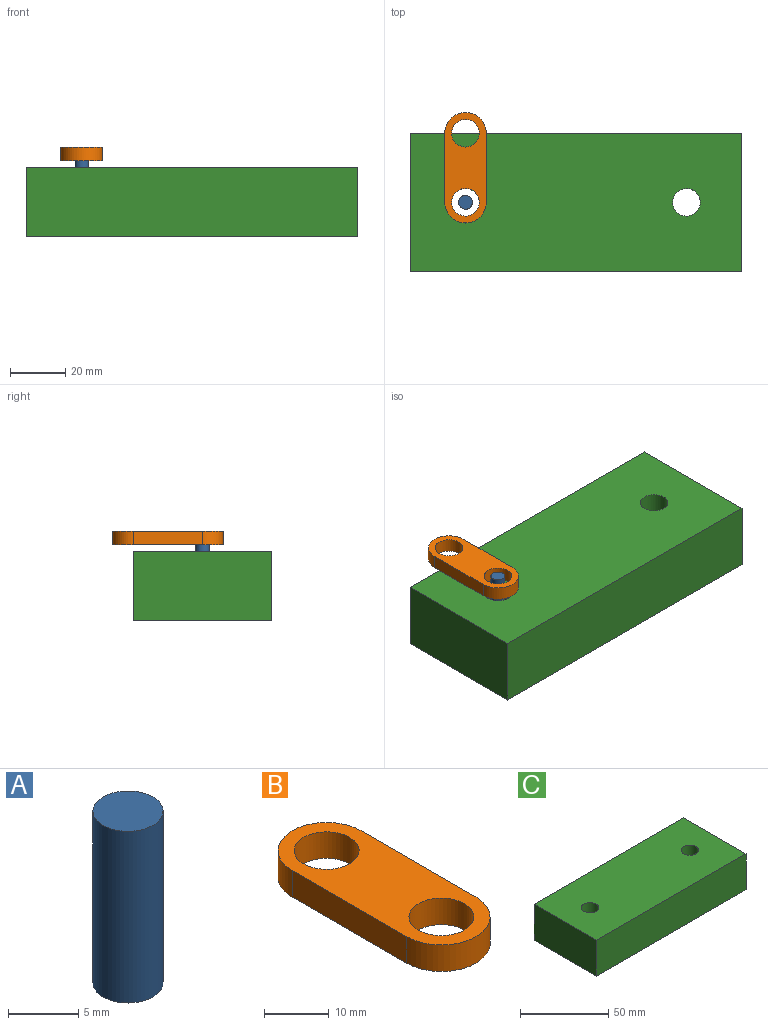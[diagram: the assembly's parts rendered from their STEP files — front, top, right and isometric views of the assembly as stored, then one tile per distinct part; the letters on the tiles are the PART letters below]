
ASSEMBLY  parts=3 mates=2
PART A: 3 faces, bbox 5x5x15 mm
  f0: plane 5x5mm, normal (0,0,-1), area 19.6mm2, adj f1
  f1: cylinder r=2.5mm len=15mm, axis (0,0,1), area 235.6mm2, adj f0,f2
  f2: plane 5x5mm, normal (0,0,1), area 19.6mm2, adj f1
PART B: 8 faces, bbox 15x40x5 mm
  f0: plane 25x5mm, normal (-1,0,0), area 125mm2, adj f1,f5,f6,f7
  f1: cylinder r=7.5mm len=15mm, axis (0,0,-1), area 117.8mm2, adj f0,f2,f6,f7
  f2: plane 25x5mm, normal (1,0,0), area 125mm2, adj f1,f5,f6,f7
  f3: cylinder r=5mm len=10mm, axis (0,0,-1), area 157.1mm2, adj f6,f7
  f4: cylinder r=5mm len=10mm, axis (0,0,-1), area 157.1mm2, adj f6,f7
  f5: cylinder r=7.5mm len=15mm, axis (0,0,-1), area 117.8mm2, adj f0,f2,f6,f7
  f6: plane 40x15mm, normal (0,0,1), area 394.6mm2, adj f0,f1,f2,f3,f4,f5
  f7: plane 40x15mm, normal (0,0,-1), area 394.6mm2, adj f0,f1,f2,f3,f4,f5
PART C: 8 faces, bbox 120x50x25 mm
  f0: plane 50x25mm, normal (1,0,0), area 1250mm2, adj f1,f4,f6,f7
  f1: plane 120x25mm, normal (0,1,0), area 3000mm2, adj f0,f2,f6,f7
  f2: plane 50x25mm, normal (-1,0,0), area 1250mm2, adj f1,f4,f6,f7
  f3: cylinder r=5mm len=25mm, axis (0,0,-1), area 785.4mm2, adj f6,f7
  f4: plane 120x25mm, normal (0,-1,0), area 3000mm2, adj f0,f2,f6,f7
  f5: cylinder r=5mm len=25mm, axis (0,0,-1), area 785.4mm2, adj f6,f7
  f6: plane 120x50mm, normal (0,0,1), area 5842.9mm2, adj f0,f1,f2,f3,f4,f5
  f7: plane 120x50mm, normal (0,0,-1), area 5842.9mm2, adj f0,f1,f2,f3,f4,f5
PLACE A t=(36.45,-14.85,-5.45)mm
PLACE B t=(36.45,10.15,4.55)mm
PLACE C t=(36.45,10.15,7.05)mm
MATE revolute A.f1 <-> C.f3  axis (0,0,1) through (-3.55,10.15,32.05)mm
MATE revolute A.f1 <-> B.f3  axis (0,0,1) through (-3.55,10.15,39.55)mm
